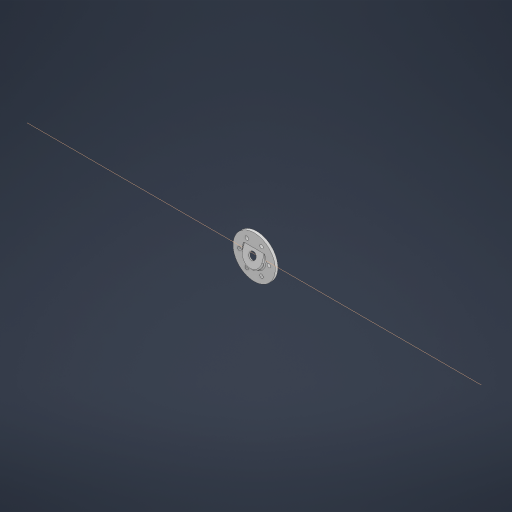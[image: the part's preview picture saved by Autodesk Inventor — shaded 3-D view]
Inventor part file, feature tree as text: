
AUTODESK INVENTOR PART (.ipt)
format: ipt  version: 2024.1 (Build 281209000, 209)  size: 512,000 bytes
history: native  units: in
note: dims shown in document units (in); Inventor stores cm internally (conversion verified against a paired STEP export)
features: extrude x10, sketch x8, projected_geometry x7, other x5, plane x3, fillet x2, reference x2, chamfer x1
ambient origin geometry x8: Origin, YZ Plane, XZ Plane, XY Plane, X Axis, Y Axis, Z Axis, Center Point
bodies: Solid1 (feature_tree)
feature tree (38):
  plane  "Work Plane1"
  sketch  "Sketch1"  dims[d0=0.1654in d1=0.1654in]
  extrude  "Extrusion1"  Depth=0.1654in
  extrude  "Extrusion2"  Depth=0.1654in
  plane  "Work Plane2"
  other  "Work Axis1"
  sketch  "Sketch2"  dims[d2=0.1654in d3=0.1654in]
  extrude  "Extrusion3"  Depth=0.1654in
  extrude  "Extrusion4"  Depth=2.0in
  extrude  "Extrusion5"  Depth=0.25in TaperAngle=0.0deg
  extrude  "Extrusion6"  TaperAngle=0.0deg  [1 undecoded]
  fillet  "Fillet1"  Radius=0.08in
  sketch  "Sketch4"  dims[d6=0.002in d7=2.0in]
  extrude  "Extrusion7"  Depth=0.3425in
  extrude  "Extrusion8"  Depth=0.03in TaperAngle=0.0deg
  plane  "Work Plane3"
  extrude  "Extrusion9"  Depth=0.03in
  chamfer  "Chamfer2"  Distance=0.375in
  extrude  "Extrusion10"  TaperAngle=0.0deg  [1 undecoded]
  fillet  "Fillet2"  Radius=0.87in
  reference  "Reference1"
  reference  "Reference2"
  sketch  "Sketch3"  dims[d4=0.1654in d5=0.1654in]
  projected_geometry  "Projected Loop1"
  projected_geometry  "Projected Loop2"
  sketch  "Sketch5"  dims[d8=0.125in d9=0.0in d10=0.25in d11=0.0in]
  projected_geometry  "Projected Loop3"
  sketch  "Sketch6"  dims[d12=0.002in d13=0.0in d14=0.0in d15=0.08in]
  projected_geometry  "Projected Loop4"
  projected_geometry  "Projected Loop5"
  sketch  "Sketch7"  dims[d16=1.0in d17=0.0in d18=0.3425in]
  sketch  "Sketch8"  dims[d19=0.0625in d20=0.0in d24=0.0625in d25=0.0in d26=0.05in d27=0.375in d28=0.0in d29=0.0in d30=0.0in d31=0.87in d32=0.2756in d33=0.0in d34=0.0in d35=0.025in d36=0.125in d37=45.0deg d38=0.0in d39=0.0in d40=0.03in d41=0.0in d42=0.0in d43=0.0in d44=0.0in]
  projected_geometry  "Projected Loop6"
  projected_geometry  "Projected Loop7"
  other  "<userpath>\Documents\School\FallCAD\Trebuchet\Trebuchet.iam"
  other  "Trebuchet.iam"
  other  "FrameTop:5"
  other  "BallBearing_8x22x7mm:10"
note: 2 required parameter values undecoded (feature->parameter linkage not recoverable at this tier; creation-order binding heuristic only, values carry confidence <= 0.55)
